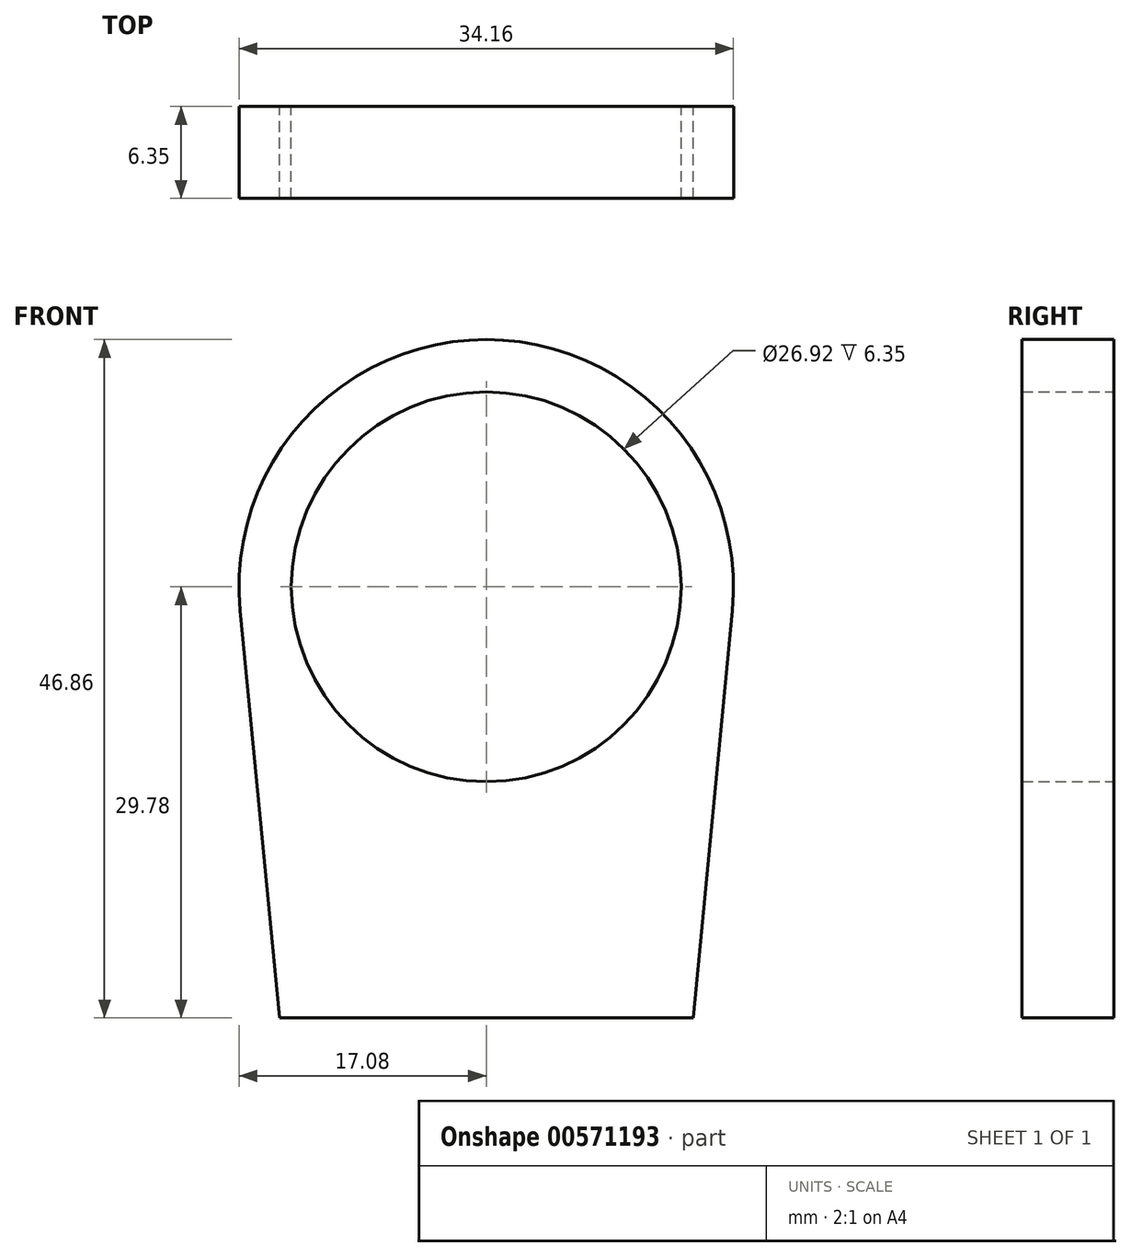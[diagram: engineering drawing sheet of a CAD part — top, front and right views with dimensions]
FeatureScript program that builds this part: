
annotation { "Feature Type Name" : "Feature", "Feature Type Description" : "" }
export const myFeature = defineFeature(function(context is Context, id is Id, definition is map)
    precondition{}
    {
        {
            var Q0;
            Q0=qCreatedBy(makeId("Front.planeOp"),FACE);
            var sketch = newSketch(context, id + "F0", { "sketchPlane" : qUnion([Q0])});
            skArc(sketch, "E0", {"start": v(17, -1.64) * mm, "mid": v(0, 17.08) * mm, "end": v(-17, -1.64) * mm});
            skLineSegment(sketch, "E1", {"start": v(-14.29, -29.78) * mm, "end": v(14.29, -29.78) * mm});
            skLineSegment(sketch, "E2", {"start": v(-14.29, -29.78) * mm, "end": v(-17.16, 0) * mm});
            skLineSegment(sketch, "E3", {"start": v(14.29, -29.78) * mm, "end": v(17.16, 0) * mm});
            skCircle(sketch, "E4", {"center": v(0, 0) * mm, "radius": 13.46 * mm});
            skSolve(sketch);
        }
        {
            var Q0;
            Q0=qSketchRegion(id+"F0",true);
            extrude(context, id + "F1", {"entities" : qUnion([Q0]), "depth" : 6.35 * mm});
        }
    });
